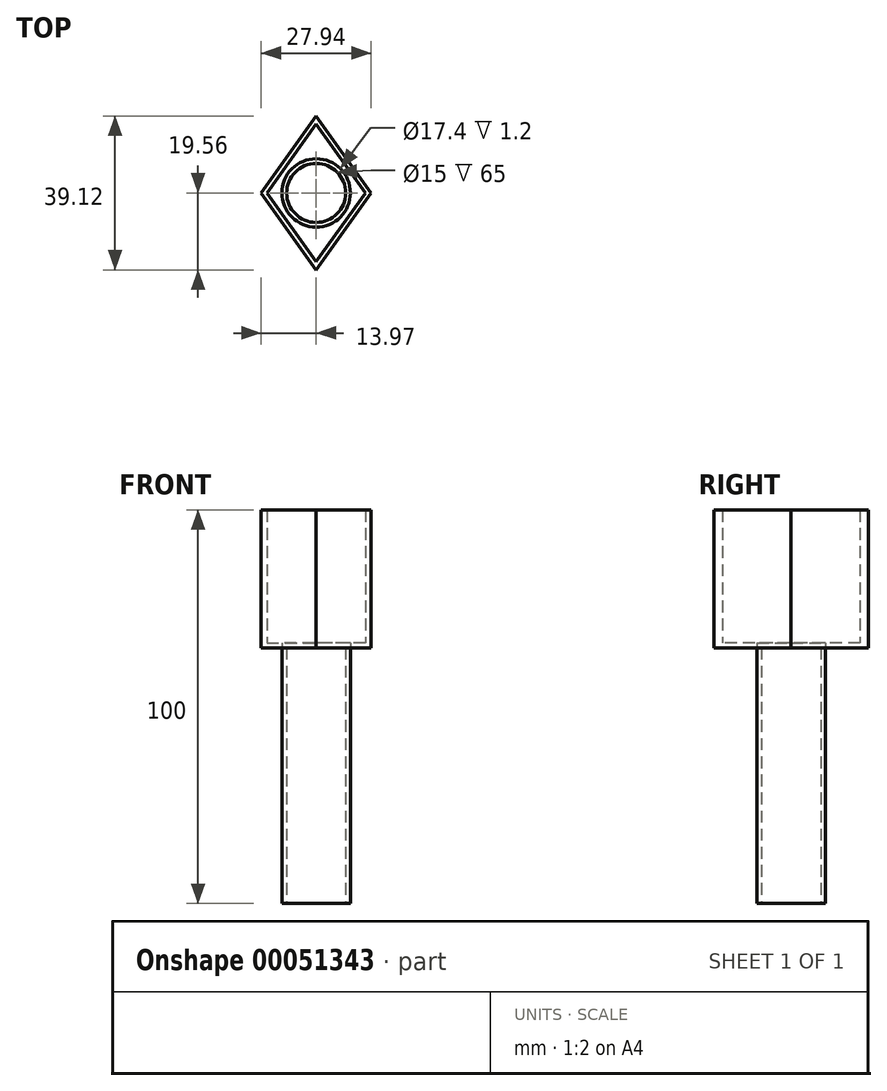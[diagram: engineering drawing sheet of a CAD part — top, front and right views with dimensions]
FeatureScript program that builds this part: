
annotation { "Feature Type Name" : "Feature", "Feature Type Description" : "" }
export const myFeature = defineFeature(function(context is Context, id is Id, definition is map)
    precondition{}
    {
        {
            var Q0;
            Q0=qCreatedBy(makeId("Top.planeOp"),FACE);
            var sketch = newSketch(context, id + "F0", { "sketchPlane" : qUnion([Q0])});
            skCircle(sketch, "E0", {"center": v(0, 0) * mm, "radius": 7.5 * mm});
            skCircle(sketch, "E1.0", {"center": v(0, 0) * mm, "radius": 8.7 * mm});
            skSolve(sketch);
        }
        {
            var Q0;
            Q0 = qSketchRegion(id + "F0", true);
            extrude(context, id + "F1", {"entities" : qUnion([Q0]), "depth" : 65 * mm});
        }
        {
            var Q0;
            Q0=makeQuery(id+"F1.opExtrude","CAP_FACE",FACE,{"disambiguationData":[OSD([sQuery(id+"F0.wireOp",EDGE,"E0"),sQuery(id+"F0.wireOp",EDGE,"E1.0")])],"isStart":false});
            var sketch = newSketch(context, id + "F2", { "sketchPlane" : qUnion([Q0])});
            skLineSegment(sketch, "E2", {"start": v(0, 0) * mm, "end": v(0, 17.5) * mm});
            skLineSegment(sketch, "E3", {"start": v(0, 17.5) * mm, "end": v(-12.5, 0) * mm});
            skLineSegment(sketch, "E4", {"start": v(-12.5, 0) * mm, "end": v(0, -17.5) * mm});
            skLineSegment(sketch, "E5", {"start": v(0, -17.5) * mm, "end": v(12.5, 0) * mm});
            skLineSegment(sketch, "E6", {"start": v(12.5, 0) * mm, "end": v(0, 17.5) * mm});
            skLineSegment(sketch, "E7", {"start": v(0, 0) * mm, "end": v(0, -17.5) * mm});
            skLineSegment(sketch, "E8.0", {"start": v(0, 19.56) * mm, "end": v(-13.97, 0) * mm});
            skLineSegment(sketch, "E8.1", {"start": v(13.97, 0) * mm, "end": v(0, 19.56) * mm});
            skLineSegment(sketch, "E8.2", {"start": v(0, -19.56) * mm, "end": v(13.97, 0) * mm});
            skLineSegment(sketch, "E8.3", {"start": v(-13.97, 0) * mm, "end": v(0, -19.56) * mm});
            skSolve(sketch);
        }
        {
            var Q0;
            Q0 = qSketchRegion(id + "F2", true);
            extrude(context, id + "F3", {"entities" : qUnion([Q0]), "depth" : 35 * mm});
        }
        {
            var Q0;
            {var subQ4=sQuery(id+"F2.wireOp",EDGE,"E3");Q0=makeQuery(id+"F2.imprint","IMPRINT",FACE,{"disambiguationData":[TD([[makeQuery(id+"F2.imprint","IMPRINT",EDGE,{"derivedFrom":subQ4}),1.0]])]});}
            var Q1;
            {var subQ1=sQuery(id+"F2.wireOp",EDGE,"E5");Q1=makeQuery(id+"F2.imprint","IMPRINT",FACE,{"disambiguationData":[TD([[makeQuery(id+"F2.imprint","IMPRINT",EDGE,{"derivedFrom":subQ1}),1.0]])]});}
            extrude(context, id + "F4", {"entities" : qUnion([Q0, Q1]), "operationType" : NewBodyOperationType.ADD, "depth" : 1.2 * mm});
        }
    });
